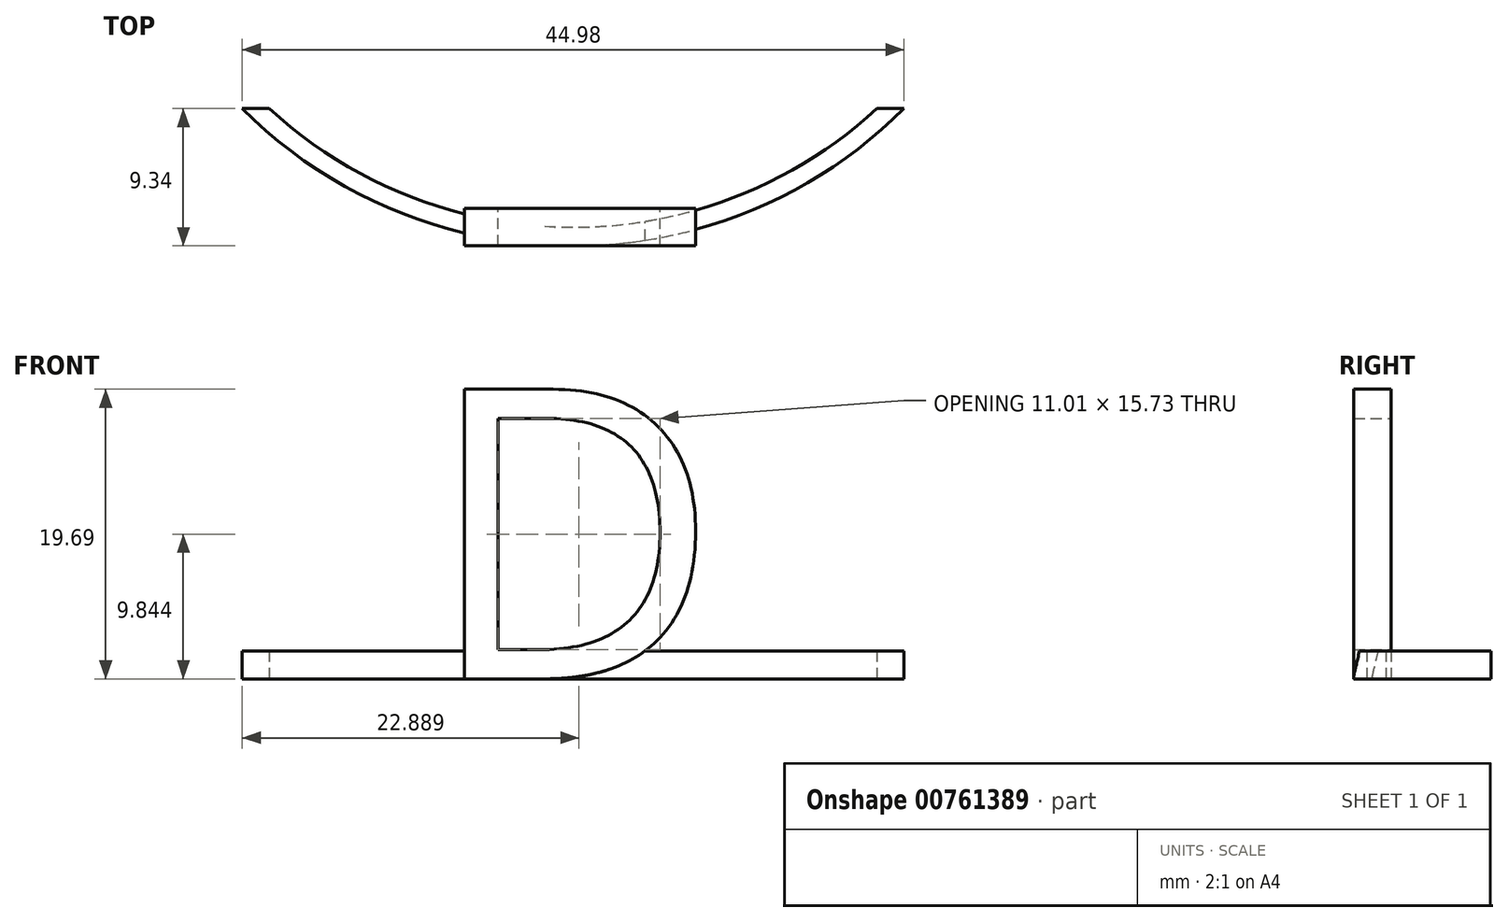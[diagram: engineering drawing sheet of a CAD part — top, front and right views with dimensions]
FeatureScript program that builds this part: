
annotation { "Feature Type Name" : "Feature", "Feature Type Description" : "" }
export const myFeature = defineFeature(function(context is Context, id is Id, definition is map)
    precondition{}
    {
        {
            var Q0;
            Q0=qCreatedBy(makeId("Front.planeOp"),FACE);
            var sketch = newSketch(context, id + "F0", { "sketchPlane" : qUnion([Q0])});
            skText(sketch, "E0", { "text": "D", "fontName": "OpenSans-Regular.ttf"});
            const initialGuessF0  = {"E0": [-0.0101, 0, 1, 0, 0.01986]};
            skSetInitialGuess(sketch, initialGuessF0);
            skSolve(sketch);
        }
        {
            var Q0;
            Q0 = qSketchRegion(id + "F0", true);
            extrude(context, id + "F1", {"entities" : qUnion([Q0]), "depth" : 2.54 * mm, "offsetDistance" : 25.4 * mm});
        }
        {
            var Q0;
            Q0=qCreatedBy(makeId("Top.planeOp"),FACE);
            var sketch = newSketch(context, id + "F2", { "sketchPlane" : qUnion([Q0])});
            skCircle(sketch, "E1", {"center": v(0, 29.21) * mm, "radius": 31.75 * mm});
            skCircle(sketch, "E2.0", {"center": v(0, 29.21) * mm, "radius": 30.48 * mm});
            skSolve(sketch);
        }
        {
            var Q0;
            Q0=makeQuery(id+"F2.imprint","IMPRINT",FACE,{"disambiguationData":[TD([[makeQuery(id+"F2.imprint","IMPRINT",EDGE,{"derivedFrom":sQuery(id+"F2.wireOp",EDGE,"E1")}),1.0]])]});
            extrude(context, id + "F3", {"entities" : qUnion([Q0]), "operationType" : NewBodyOperationType.ADD, "depth" : 1.9 * mm, "offsetDistance" : 25.4 * mm});
        }
        {
            var Q0;
            Q0=makeQuery(id+"F3.opExtrude","CAP_FACE",FACE,{"disambiguationData":[OSD([sQuery(id+"F2.wireOp",EDGE,"E1")])],"isStart":false});
            var sketch = newSketch(context, id + "F4", { "sketchPlane" : qUnion([Q0])});
            skLineSegment(sketch, "E3.bottom", {"start": v(-36.34, 6.8) * mm, "end": v(40.88, 6.8) * mm});
            skLineSegment(sketch, "E3.top", {"start": v(-36.34, 63.95) * mm, "end": v(40.88, 63.95) * mm});
            skLineSegment(sketch, "E3.left", {"start": v(-36.34, 6.8) * mm, "end": v(-36.34, 63.95) * mm});
            skLineSegment(sketch, "E3.right", {"start": v(40.88, 6.8) * mm, "end": v(40.88, 63.95) * mm});
            skSolve(sketch);
        }
        {
            var Q0;
            Q0 = qSketchRegion(id + "F4", true);
            extrude(context, id + "F5", {"entities" : qUnion([Q0]), "operationType" : NewBodyOperationType.REMOVE, "oppositeDirection" : true, "depth" : 6.35 * mm, "offsetDistance" : 25.4 * mm});
        }
    });
